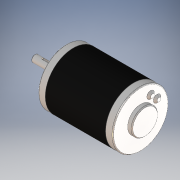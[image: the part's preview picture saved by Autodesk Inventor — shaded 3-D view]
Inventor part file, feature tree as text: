
AUTODESK INVENTOR PART (.ipt)
format: ipt  version: 2016 (Build 200138000, 138)  size: 171,520 bytes
history: native  units: in
note: dims shown in document units (in); Inventor stores cm internally (conversion verified against a paired STEP export)
features: chamfer x1
ambient origin geometry x8: Origin, YZ Plane, XZ Plane, XY Plane, X Axis, Y Axis, Z Axis, Center Point
bodies: Solid1 (feature_tree)
feature tree (1):
  chamfer  "Chamfer3"  [1 undecoded]
note: 1 required parameter value undecoded (feature->parameter linkage not recoverable at this tier; creation-order binding heuristic only, values carry confidence <= 0.55)
